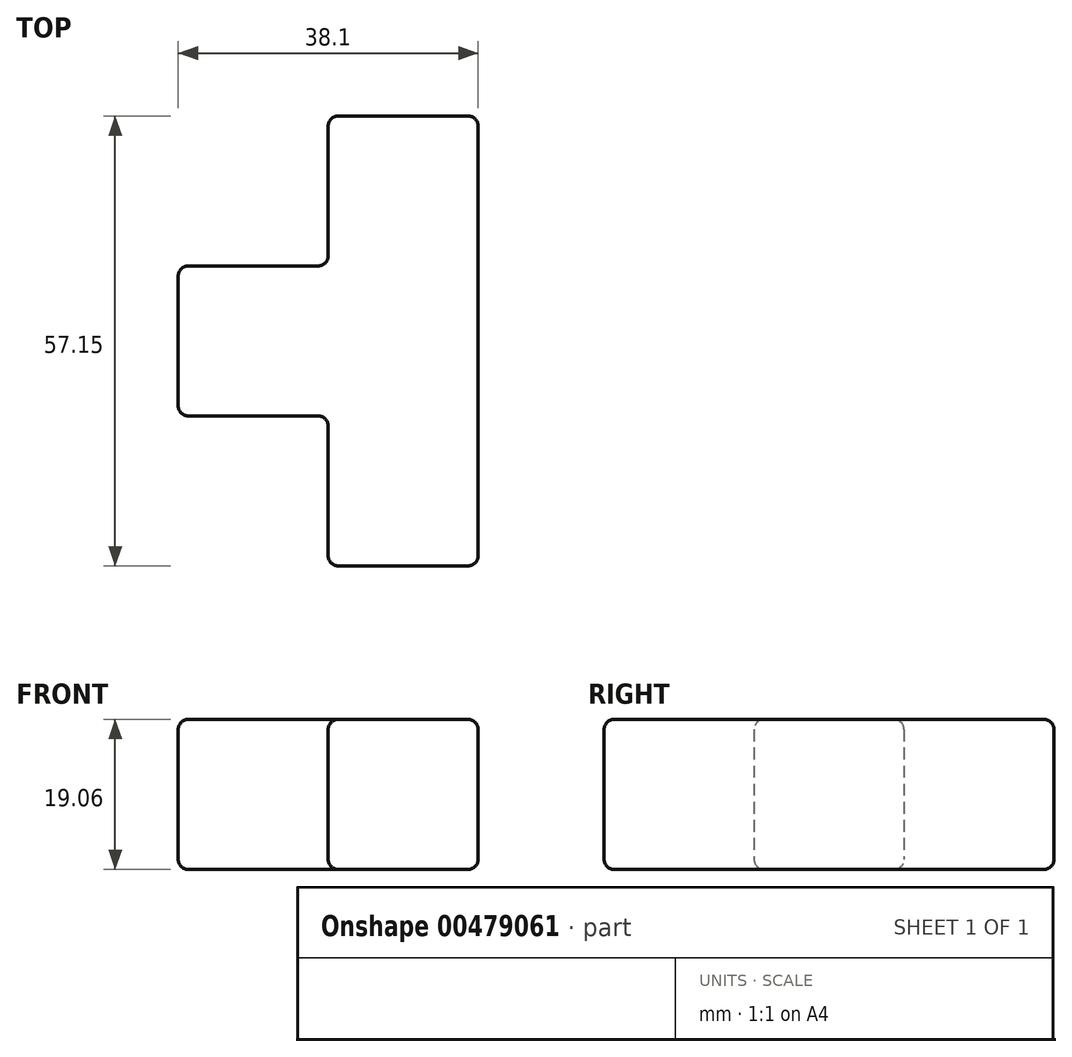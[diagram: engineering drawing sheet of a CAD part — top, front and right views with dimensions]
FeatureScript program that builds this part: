
annotation { "Feature Type Name" : "Feature", "Feature Type Description" : "" }
export const myFeature = defineFeature(function(context is Context, id is Id, definition is map)
    precondition{}
    {
        {
            var Q0;
            Q0=qCreatedBy(makeId("Top.planeOp"),FACE);
            var sketch = newSketch(context, id + "F0", { "sketchPlane" : qUnion([Q0])});
            skLineSegment(sketch, "E0.bottom", {"start": v(0, 16.14) * mm, "end": v(19.05, 16.14) * mm});
            skLineSegment(sketch, "E0.top", {"start": v(0, -41.01) * mm, "end": v(19.05, -41.01) * mm});
            skLineSegment(sketch, "E0.left", {"start": v(0, 16.14) * mm, "end": v(0, -2.91) * mm});
            skLineSegment(sketch, "E0.right", {"start": v(19.05, 16.14) * mm, "end": v(19.05, -41.01) * mm});
            skLineSegment(sketch, "E1.bottom", {"start": v(0, -2.91) * mm, "end": v(-19.05, -2.91) * mm});
            skLineSegment(sketch, "E1.top", {"start": v(0, -21.96) * mm, "end": v(-19.05, -21.96) * mm});
            skLineSegment(sketch, "E1.right", {"start": v(-19.05, -2.91) * mm, "end": v(-19.05, -21.96) * mm});
            skLineSegment(sketch, "E2.trimOffspring", {"start": v(0, -21.96) * mm, "end": v(0, -41.01) * mm});
            skSolve(sketch);
        }
        {
            var Q0;
            Q0 = qSketchRegion(id + "F0", true);
            extrude(context, id + "F1", {"entities" : qUnion([Q0]), "endBound" : BoundingType.SYMMETRIC, "depth" : 19.05 * mm});
        }
        {
            var Q0;
            Q0=makeQuery(id+"F1.opExtrude","SWEPT_FACE",FACE,{"disambiguationData":[OSD([sQuery(id+"F0.wireOp",EDGE,"E0.right")])]});
            var Q1;
            Q1=makeQuery(id+"F1.opExtrude","SWEPT_FACE",FACE,{"disambiguationData":[OSD([sQuery(id+"F0.wireOp",EDGE,"E0.bottom")])]});
            var Q2;
            Q2=makeQuery(id+"F1.opExtrude","CAP_FACE",FACE,{"disambiguationData":[OSD([sQuery(id+"F0.wireOp",EDGE,"E0.bottom"),sQuery(id+"F0.wireOp",EDGE,"E0.top"),sQuery(id+"F0.wireOp",EDGE,"E0.left"),sQuery(id+"F0.wireOp",EDGE,"E0.right"),sQuery(id+"F0.wireOp",EDGE,"E1.bottom"),sQuery(id+"F0.wireOp",EDGE,"E1.top"),sQuery(id+"F0.wireOp",EDGE,"E1.right"),sQuery(id+"F0.wireOp",EDGE,"E2.trimOffspring")])],"isStart":false});
            var Q3;
            Q3=makeQuery(id+"F1.opExtrude","CAP_FACE",FACE,{"disambiguationData":[OSD([sQuery(id+"F0.wireOp",EDGE,"E0.bottom"),sQuery(id+"F0.wireOp",EDGE,"E0.top"),sQuery(id+"F0.wireOp",EDGE,"E0.left"),sQuery(id+"F0.wireOp",EDGE,"E0.right"),sQuery(id+"F0.wireOp",EDGE,"E1.bottom"),sQuery(id+"F0.wireOp",EDGE,"E1.top"),sQuery(id+"F0.wireOp",EDGE,"E1.right"),sQuery(id+"F0.wireOp",EDGE,"E2.trimOffspring")])],"isStart":true});
            var Q4;
            Q4=makeQuery(id+"F1.opExtrude","SWEPT_FACE",FACE,{"disambiguationData":[OSD([sQuery(id+"F0.wireOp",EDGE,"E1.right")])]});
            var Q5;
            Q5=makeQuery(id+"F1.opExtrude","SWEPT_FACE",FACE,{"disambiguationData":[OSD([sQuery(id+"F0.wireOp",EDGE,"E0.top")])]});
            var Q6;
            Q6=makeQuery(id+"F1.opExtrude","SWEPT_FACE",FACE,{"disambiguationData":[OSD([sQuery(id+"F0.wireOp",EDGE,"E0.left")])]});
            var Q7;
            Q7=makeQuery(id+"F1.opExtrude","SWEPT_FACE",FACE,{"disambiguationData":[OSD([sQuery(id+"F0.wireOp",EDGE,"E1.bottom")])]});
            var Q8;
            Q8=makeQuery(id+"F1.opExtrude","SWEPT_FACE",FACE,{"disambiguationData":[OSD([sQuery(id+"F0.wireOp",EDGE,"E2.trimOffspring")])]});
            var Q9;
            Q9=makeQuery(id+"F1.opExtrude","SWEPT_FACE",FACE,{"disambiguationData":[OSD([sQuery(id+"F0.wireOp",EDGE,"E1.top")])]});
            fillet(context, id + "F2", {"entities" : qUnion([Q0, Q1, Q2, Q3, Q4, Q5, Q6, Q7, Q8, Q9]), "radius" : 1.27 * mm, "tangentPropagation" : true, "allowEdgeOverflow" : false});
        }
    });
